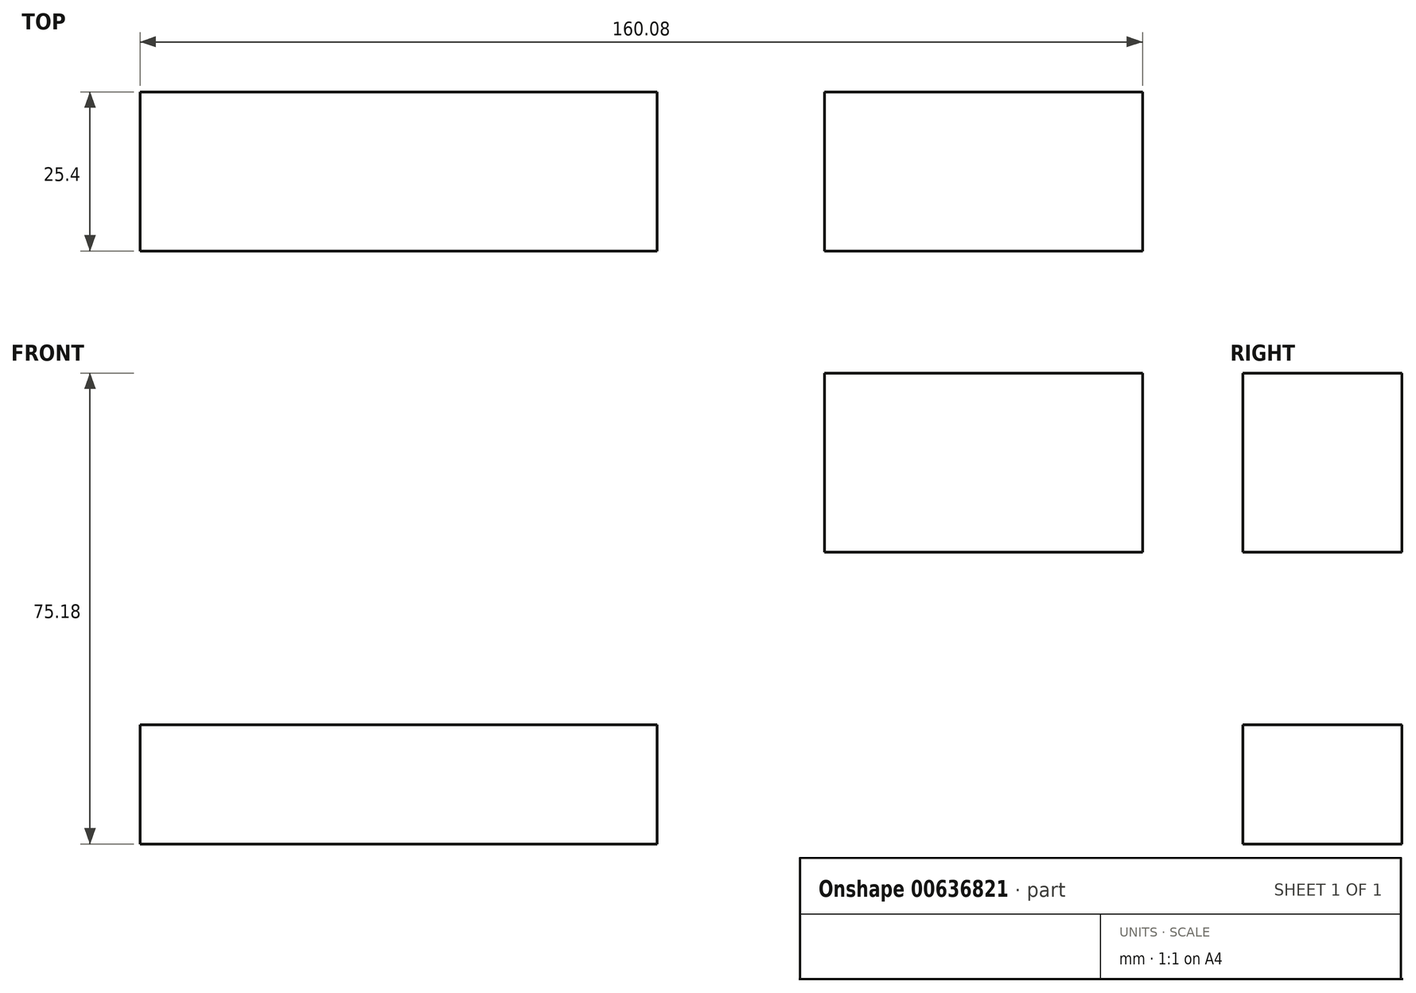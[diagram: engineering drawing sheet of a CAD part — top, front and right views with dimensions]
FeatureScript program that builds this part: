
annotation { "Feature Type Name" : "Feature", "Feature Type Description" : "" }
export const myFeature = defineFeature(function(context is Context, id is Id, definition is map)
    precondition{}
    {
        {
            var Q0;
            Q0=qCreatedBy(makeId("Front.planeOp"),FACE);
            var sketch = newSketch(context, id + "F0", { "sketchPlane" : qUnion([Q0])});
            skLineSegment(sketch, "E0.bottom", {"start": v(-41.28, 9.52) * mm, "end": v(41.27, 9.53) * mm});
            skLineSegment(sketch, "E0.top", {"start": v(-41.28, -9.53) * mm, "end": v(41.28, -9.53) * mm});
            skLineSegment(sketch, "E0.left", {"start": v(-41.28, 9.52) * mm, "end": v(-41.28, -9.53) * mm});
            skLineSegment(sketch, "E0.right", {"start": v(41.27, 9.53) * mm, "end": v(41.28, -9.52) * mm});
            skPoint(sketch, "E0.middle", {"position": v(0, 0) * mm});
            skLineSegment(sketch, "E1.bottom", {"start": v(68.01, 37.08) * mm, "end": v(118.81, 37.08) * mm});
            skLineSegment(sketch, "E1.top", {"start": v(68.01, 65.65) * mm, "end": v(118.81, 65.65) * mm});
            skLineSegment(sketch, "E1.left", {"start": v(68.01, 37.08) * mm, "end": v(68.01, 65.65) * mm});
            skLineSegment(sketch, "E1.right", {"start": v(118.81, 37.08) * mm, "end": v(118.81, 65.65) * mm});
            skPoint(sketch, "E1.middle", {"position": v(93.41, 51.37) * mm});
            skLineSegment(sketch, "E2", {"start": v(41.27, 9.53) * mm, "end": v(41.27, 41.66) * mm});
            skArc(sketch, "E3", {"start": v(41.27, 41.66) * mm, "mid": v(46.99, 53.85) * mm, "end": v(60.02, 57.27) * mm});
            skLineSegment(sketch, "E4", {"start": v(60.02, 57.27) * mm, "end": v(93.03, 57.27) * mm});
            skSolve(sketch);
        }
        {
            var Q0;
            Q0 = qSketchRegion(id + "F0", true);
            extrude(context, id + "F1", {"entities" : qUnion([Q0]), "depth" : 25.4 * mm, "offsetDistance" : 25.4 * mm});
        }
    });
